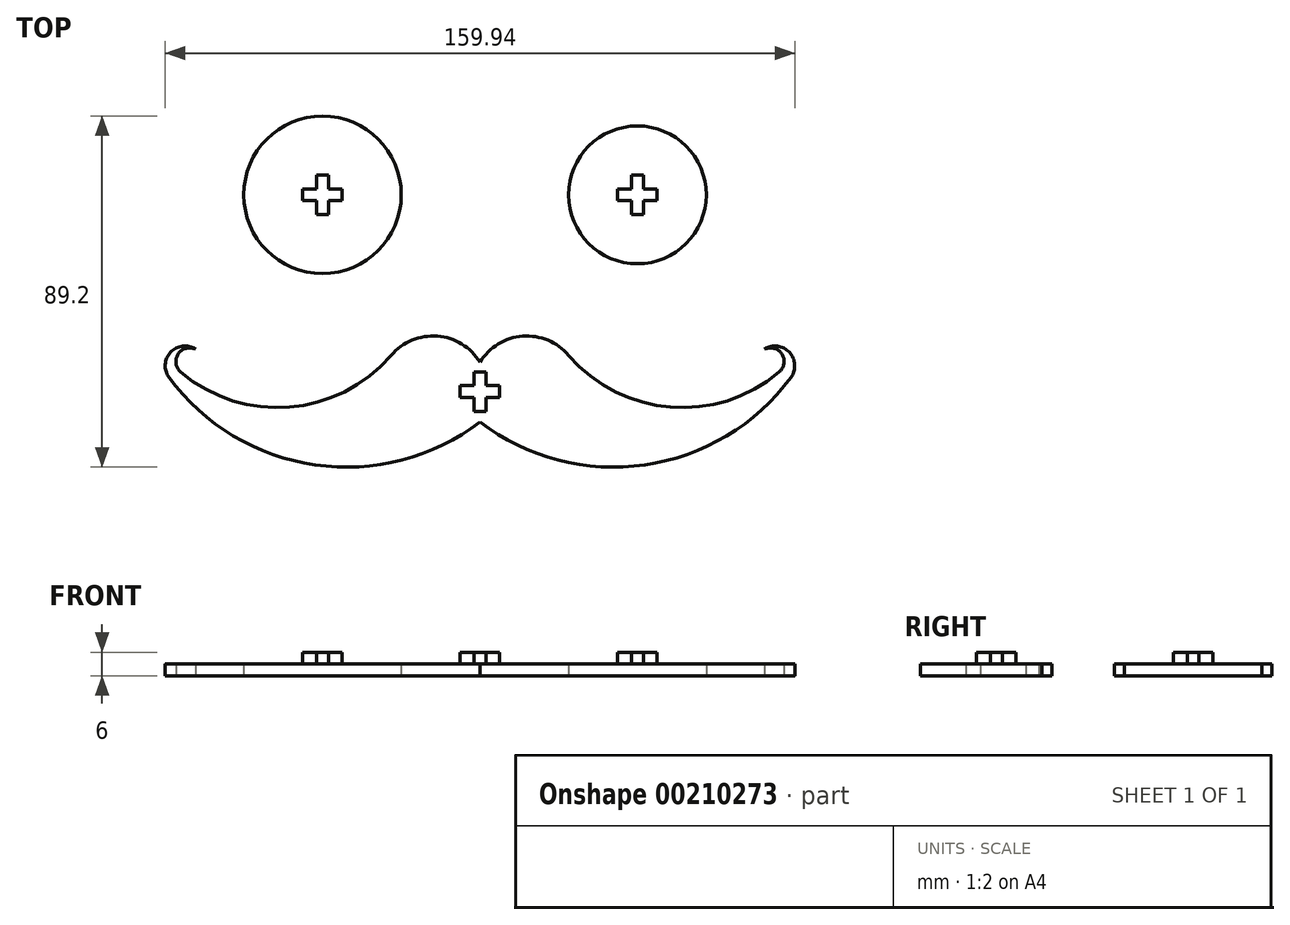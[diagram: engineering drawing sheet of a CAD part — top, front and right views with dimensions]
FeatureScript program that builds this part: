
annotation { "Feature Type Name" : "Feature", "Feature Type Description" : "" }
export const myFeature = defineFeature(function(context is Context, id is Id, definition is map)
    precondition{}
    {
        {
            var Q0;
            Q0=qCreatedBy(makeId("Top.planeOp"),FACE);
            var sketch = newSketch(context, id + "F0", { "sketchPlane" : qUnion([Q0])});
            skCircle(sketch, "E0", {"center": v(0, 0) * mm, "radius": 20 * mm});
            skCircle(sketch, "E1", {"center": v(80, 0) * mm, "radius": 17.5 * mm});
            skLineSegment(sketch, "E2", {"start": v(0, 0) * mm, "end": v(80, 0) * mm, "construction": true});
            skLineSegment(sketch, "E3", {"start": v(40, 0) * mm, "end": v(40, -50) * mm, "construction": true});
            skArc(sketch, "E4", {"start": v(40, -42.5) * mm, "mid": v(29.17, -35.9) * mm, "end": v(17.45, -40.77) * mm});
            skArc(sketch, "E5", {"start": v(-36.02, -45.04) * mm, "mid": v(-8.4, -53.95) * mm, "end": v(17.45, -40.77) * mm});
            skArc(sketch, "E6", {"start": v(-32.25, -39.21) * mm, "mid": v(-36.7, -40.47) * mm, "end": v(-36.02, -45.04) * mm});
            skArc(sketch, "E7", {"start": v(-32.25, -39.21) * mm, "mid": v(-38.6, -39.97) * mm, "end": v(-39, -46.36) * mm});
            skArc(sketch, "E8", {"start": v(-39, -46.36) * mm, "mid": v(-1.88, -68.63) * mm, "end": v(40, -57.7) * mm});
            skArc(sketch, "E9.MirrorCS", {"start": v(40, -42.5) * mm, "mid": v(50.83, -35.9) * mm, "end": v(62.55, -40.77) * mm});
            skArc(sketch, "E10.MirrorCS", {"start": v(116.02, -45.04) * mm, "mid": v(88.4, -53.95) * mm, "end": v(62.55, -40.77) * mm});
            skArc(sketch, "E11.MirrorCS", {"start": v(112.25, -39.21) * mm, "mid": v(116.7, -40.47) * mm, "end": v(116.02, -45.04) * mm});
            skArc(sketch, "E12.MirrorCS", {"start": v(112.25, -39.21) * mm, "mid": v(118.6, -39.97) * mm, "end": v(119, -46.36) * mm});
            skArc(sketch, "E13.MirrorCS", {"start": v(119, -46.36) * mm, "mid": v(81.88, -68.63) * mm, "end": v(40, -57.7) * mm});
            skSolve(sketch);
        }
        {
            var Q0;
            Q0=qSketchRegion(id+"F0",true);
            extrude(context, id + "F1", {"entities" : qUnion([Q0]), "depth" : 3 * mm});
        }
        {
            var Q0;
            Q0=makeQuery(id+"F1.opExtrude","CAP_FACE",FACE,{"disambiguationData":[OSD([sQuery(id+"F0.wireOp",EDGE,"E0")])],"isStart":false});
            var sketch = newSketch(context, id + "F2", { "sketchPlane" : qUnion([Q0])});
            skLineSegment(sketch, "E14.bottom", {"start": v(-1.5, 5) * mm, "end": v(1.5, 5) * mm});
            skLineSegment(sketch, "E14.top", {"start": v(-1.5, -5) * mm, "end": v(1.5, -5) * mm});
            skLineSegment(sketch, "E14.left", {"start": v(-1.5, 5) * mm, "end": v(-1.5, -5) * mm});
            skLineSegment(sketch, "E14.right", {"start": v(1.5, 5) * mm, "end": v(1.5, -5) * mm});
            skLineSegment(sketch, "E15.bottom", {"start": v(-5, 1.5) * mm, "end": v(5, 1.5) * mm});
            skLineSegment(sketch, "E15.top", {"start": v(-5, -1.5) * mm, "end": v(5, -1.5) * mm});
            skLineSegment(sketch, "E15.left", {"start": v(-5, 1.5) * mm, "end": v(-5, -1.5) * mm});
            skLineSegment(sketch, "E15.right", {"start": v(5, 1.5) * mm, "end": v(5, -1.5) * mm});
            skLineSegment(sketch, "E16", {"start": v(-5, 0) * mm, "end": v(0, 0) * mm, "construction": true});
            skPoint(sketch, "E16.endSnap0", {"position": v(0, 5) * mm});
            skLineSegment(sketch, "E17.1.0.0", {"start": v(78.5, 5) * mm, "end": v(81.5, 5) * mm});
            skLineSegment(sketch, "E17.1.0.1", {"start": v(81.5, 5) * mm, "end": v(81.5, -5) * mm});
            skLineSegment(sketch, "E17.1.0.2", {"start": v(75, 1.5) * mm, "end": v(85, 1.5) * mm});
            skLineSegment(sketch, "E17.1.0.3", {"start": v(85, 1.5) * mm, "end": v(85, -1.5) * mm});
            skLineSegment(sketch, "E17.1.0.4", {"start": v(75, -1.5) * mm, "end": v(85, -1.5) * mm});
            skLineSegment(sketch, "E17.1.0.5", {"start": v(78.5, -5) * mm, "end": v(81.5, -5) * mm});
            skLineSegment(sketch, "E17.1.0.6", {"start": v(78.5, 5) * mm, "end": v(78.5, -5) * mm});
            skLineSegment(sketch, "E17.1.0.7", {"start": v(75, 1.5) * mm, "end": v(75, -1.5) * mm});
            skLineSegment(sketch, "E17.direction1", {"start": v(-1.5, 5) * mm, "end": v(78.5, 5) * mm, "construction": true});
            skLineSegment(sketch, "E18.bottom", {"start": v(38.5, -45) * mm, "end": v(41.5, -45) * mm});
            skLineSegment(sketch, "E18.top", {"start": v(38.5, -55) * mm, "end": v(41.5, -55) * mm});
            skLineSegment(sketch, "E18.left", {"start": v(38.5, -45) * mm, "end": v(38.5, -55) * mm});
            skLineSegment(sketch, "E18.right", {"start": v(41.5, -45) * mm, "end": v(41.5, -55) * mm});
            skLineSegment(sketch, "E19.bottom", {"start": v(35, -48.5) * mm, "end": v(45, -48.5) * mm});
            skLineSegment(sketch, "E19.top", {"start": v(35, -51.5) * mm, "end": v(45, -51.5) * mm});
            skLineSegment(sketch, "E19.left", {"start": v(35, -48.5) * mm, "end": v(35, -51.5) * mm});
            skLineSegment(sketch, "E19.right", {"start": v(45, -48.5) * mm, "end": v(45, -51.5) * mm});
            skPoint(sketch, "E20", {"position": v(40, -50) * mm});
            skPoint(sketch, "E20.positionSnap0", {"position": v(40, -45) * mm});
            skPoint(sketch, "E20.positionSnap1", {"position": v(35, -50) * mm});
            skSolve(sketch);
        }
        {
            var Q0;
            Q0=qSketchRegion(id+"F2",true);
            extrude(context, id + "F3", {"entities" : qUnion([Q0]), "operationType" : NewBodyOperationType.ADD, "depth" : 3 * mm});
        }
    });
